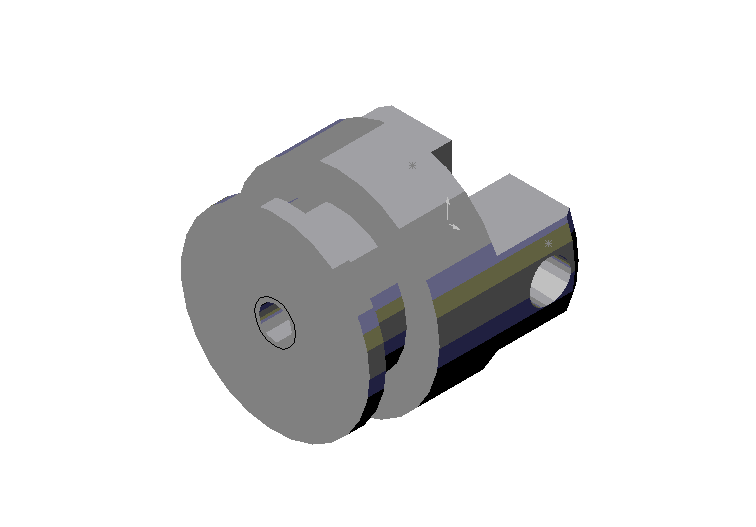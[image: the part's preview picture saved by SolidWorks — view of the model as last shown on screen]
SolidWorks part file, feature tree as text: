
SOLIDWORKS PART (.sldprt)
format: sldprt  version: not decoded by parser v0  size: 157,184 bytes
history: native  units: mm
features: sketch x9, cut_extrude x4, plane x3, material x1, extrude x1, chamfer x1, hole x1, thread x1 (+8 scaffold rows collapsed)
feature tree (29):
  scaffold x8  (default folders/planes/origin — collapsed)
  material  "Matériau <non spécifié>"
  plane  "Face"
  plane  "Dessus"
  plane  "Droite"
  sketch  "Esquisse1"  dims[D1=25.0mm]
  extrude  "Base-Extrusion"  Depth=21mm
  sketch  "Esquisse2"  dims[D1=23.0mm]
  cut_extrude  "Enlèv. mat.-Extru.1"  Depth=2mm
  sketch  "Esquisse3"  dims[D1=17.0mm]
  cut_extrude  "Enlèv. mat.-Extru.2"  Depth=5.5mm
  sketch  "Esquisse7"  dims[D1=10.0mm D2=7.0mm]
  cut_extrude  "Enlèv. mat.-Extru.7"  Depth=5.5mm
  sketch  "Esquisse6"  dims[c1.D1=~4.53415mm c1.D2=5.0mm c2.D1=5.0mm c2.D2=5.0mm c2.D3=5.0mm c3.D2=5.0mm c3.D1=4.0mm c4.D2=4.0mm c4.D3=5.5mm c5.D2=5.5mm]
  cut_extrude  "Enlèv. mat.-Extru.6"  [1 undecoded]
  chamfer  "Chanfrein1"  Distance=1mm Angle=30deg
  hole  "Perçage1"  Diameter=4mm Depth=12mm
  sketch  "Esquisse10"
  sketch  "Esquisse9"  dims[c1.D1=~97.659253deg c1.D2=~82.982399deg c1.Diamètre=4.0mm c2.D2=100.0mm c2.D3=~82.982399deg c2.D4=90.0deg c3.D3=~97.716715deg c3.Profondeur=12.0mm c3.Angle=118.0deg]
  thread  "Représentation de filetage1"  Diameter=10mm  [1 undecoded]
  sketch  "Point 3"  dims[D1=8.25mm]
  sketch  "Point 4"
decode coverage: 14 of 17 modeling features carry decoded parameters
note: ~ marks probable driven/reference dimensions
note: 2 parameter values undecoded
note: suppression state not decoded; provenance and decode notes live in map.json
